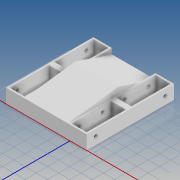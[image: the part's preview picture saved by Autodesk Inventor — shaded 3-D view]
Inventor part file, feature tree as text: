
AUTODESK INVENTOR PART (.ipt)
format: ipt  version: 2020 (Build 240168000, 168)  size: 296,448 bytes
history: native  units: mm
features: extrude x12, sketch x10
ambient origin geometry x8: Origin, YZ Plane, XZ Plane, XY Plane, X Axis, Y Axis, Z Axis, Center Point
bodies: Solid1 (feature_tree)
feature tree (22):
  extrude  "Extrusion1"  Depth=156.0mm
  extrude  "Extrusion2"  Depth=3.0mm
  extrude  "Extrusion3"  Depth=3.0mm
  extrude  "Extrusion4"  Depth=3.0mm
  extrude  "Extrusion5"  Depth=3.0mm
  extrude  "Extrusion6"  Depth=12.0mm TaperAngle=0.0deg
  extrude  "Extrusion7"  Depth=12.0mm
  extrude  "Extrusion8"  Depth=70.0mm
  extrude  "Extrusion9"  Depth=3.0mm TaperAngle=0.0deg
  sketch  "Sketch13"  dims[d22=27.0mm d23=0.0mm d24=3.0mm d25=0.0mm]
  extrude  "Extrusion10"  Depth=12.0mm
  extrude  "Extrusion11"  Depth=70.0mm
  extrude  "Extrusion12"  Depth=27.0mm TaperAngle=0.0deg
  sketch  "Sketch1"  dims[d0=84.0mm d1=156.0mm]
  sketch  "Sketch2"  dims[d2=3.0mm d3=3.0mm]
  sketch  "Sketch5"  dims[d4=3.0mm d5=3.0mm]
  sketch  "Sketch6"  dims[d6=15.0mm d7=0.0mm d8=3.0mm]
  sketch  "Sketch9"  dims[d9=3.0mm d10=3.0mm]
  sketch  "Sketch10"  dims[d11=3.0mm d12=12.0mm d13=0.0mm]
  sketch  "Sketch11"  dims[d18=3.0mm d19=12.0mm]
  sketch  "Sketch12"  dims[d20=70.0mm d21=70.0mm]
  sketch  "Sketch15"  dims[d35=70.0mm d38=12.0mm d39=70.0mm d40=27.0mm d41=0.0mm d42=3.0mm d43=0.0mm d44=10.0mm d45=0.0mm d57=32.0mm d58=0.0mm d74=32.0mm d75=0.0mm d88=10.0mm d89=0.0mm d90=10.0mm d91=0.0mm d96=10.0mm d97=0.0mm d98=16.0mm d99=0.0mm d100=11.2mm d101=6.0mm d102=16.0mm d103=11.2mm d104=6.0mm d105=55.0mm d106=10.0mm d107=5.0mm d108=15.0mm d109=10.0mm d110=5.0mm d111=15.0mm d112=10.0mm d113=5.0mm d114=15.0mm d115=10.0mm d116=5.0mm d117=16.0mm d118=11.2mm d119=6.0mm d120=16.0mm d121=11.2mm d122=6.0mm]
